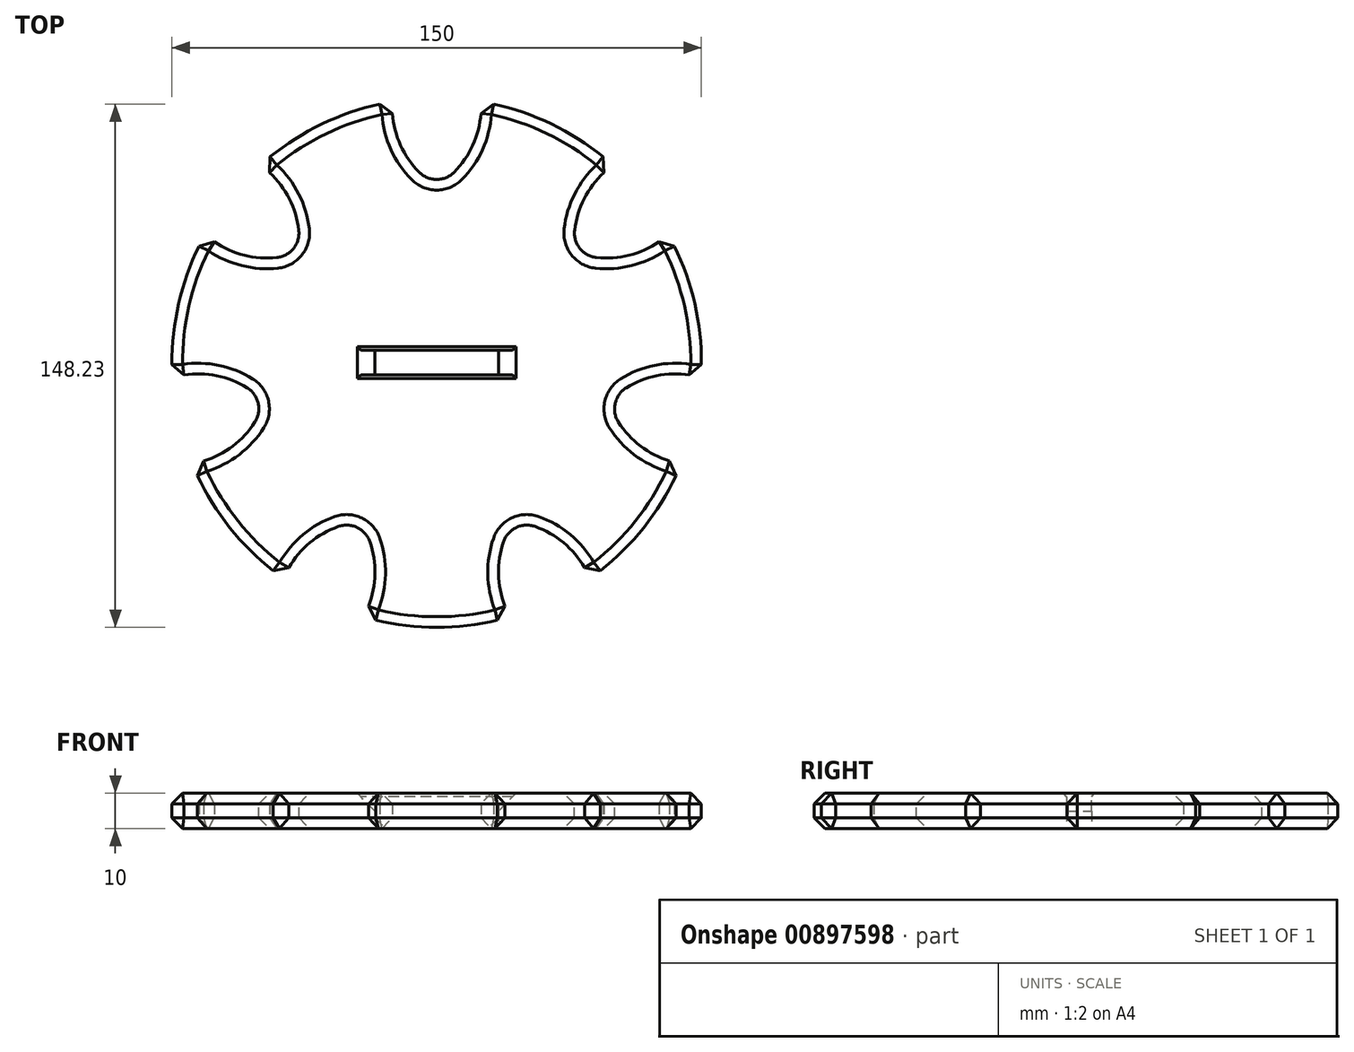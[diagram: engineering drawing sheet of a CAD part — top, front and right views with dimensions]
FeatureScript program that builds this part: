
annotation { "Feature Type Name" : "Feature", "Feature Type Description" : "" }
export const myFeature = defineFeature(function(context is Context, id is Id, definition is map)
    precondition{}
    {
        {
            var Q0;
            Q0=qCreatedBy(makeId("Top.planeOp"),FACE);
            var sketch = newSketch(context, id + "F0", { "sketchPlane" : qUnion([Q0])});
            skCircle(sketch, "E0", {"center": v(0, 0) * mm, "radius": 75 * mm});
            skLineSegment(sketch, "E1", {"start": v(0, 75) * mm, "end": v(0, 50) * mm, "construction": true});
            skLineSegment(sketch, "E2", {"start": v(0, 75) * mm, "end": v(12.5, 75) * mm, "construction": true});
            skLineSegment(sketch, "E3", {"start": v(0, 75) * mm, "end": v(-12.5, 75) * mm, "construction": true});
            skArc(sketch, "E4", {"start": v(-12.5, 75) * mm, "mid": v(-9.82, 60.71) * mm, "end": v(0, 50) * mm});
            skArc(sketch, "E5.MirrorCS", {"start": v(12.5, 75) * mm, "mid": v(9.82, 60.71) * mm, "end": v(0, 50) * mm});
            skLineSegment(sketch, "E6", {"start": v(-12.5, 75) * mm, "end": v(12.5, 75) * mm});
            skArc(sketch, "E7.1.0", {"start": v(-50.84, 56.53) * mm, "mid": v(-41.34, 45.53) * mm, "end": v(-39.1, 31.17) * mm});
            skArc(sketch, "E7.1.1", {"start": v(-66.43, 36.99) * mm, "mid": v(-53.6, 30.17) * mm, "end": v(-39.1, 31.17) * mm});
            skArc(sketch, "E7.2.0", {"start": v(-75.9, -4.5) * mm, "mid": v(-61.38, -3.93) * mm, "end": v(-48.75, -11.13) * mm});
            skArc(sketch, "E7.2.1", {"start": v(-70.34, -28.88) * mm, "mid": v(-57, -23.09) * mm, "end": v(-48.75, -11.13) * mm});
            skArc(sketch, "E7.3.0", {"start": v(-43.8, -62.15) * mm, "mid": v(-35.2, -50.44) * mm, "end": v(-21.7, -45.05) * mm});
            skArc(sketch, "E7.3.1", {"start": v(-21.28, -73) * mm, "mid": v(-17.5, -58.96) * mm, "end": v(-21.7, -45.05) * mm});
            skArc(sketch, "E7.4.0", {"start": v(21.28, -73) * mm, "mid": v(17.5, -58.96) * mm, "end": v(21.7, -45.05) * mm});
            skArc(sketch, "E7.4.1", {"start": v(43.8, -62.15) * mm, "mid": v(35.2, -50.44) * mm, "end": v(21.7, -45.05) * mm});
            skArc(sketch, "E7.5.0", {"start": v(70.34, -28.88) * mm, "mid": v(57, -23.09) * mm, "end": v(48.75, -11.13) * mm});
            skArc(sketch, "E7.5.1", {"start": v(75.9, -4.5) * mm, "mid": v(61.38, -3.93) * mm, "end": v(48.75, -11.13) * mm});
            skArc(sketch, "E7.6.0", {"start": v(66.43, 36.99) * mm, "mid": v(53.6, 30.17) * mm, "end": v(39.1, 31.17) * mm});
            skArc(sketch, "E7.6.1", {"start": v(50.84, 56.53) * mm, "mid": v(41.34, 45.53) * mm, "end": v(39.1, 31.17) * mm});
            skSolve(sketch);
        }
        {
            var Q0;
            {var subQ3=sQuery(id+"F0.wireOp",EDGE,"E0");var subQ22=sQuery(id+"F0.wireOp",EDGE,"E7.6.1");var subQ23=makeQuery(id+"F0.imprint","INTERSECT",VERTEX,{"derivedFrom":[subQ3,subQ22]});Q0=makeQuery(id+"F0.imprint","IMPRINT",FACE,{"disambiguationData":[TD([[makeQuery(id+"F0.imprint","IMPRINT",EDGE,{"disambiguationData":[TD([[subQ23,-1.0]])],"derivedFrom":subQ3}),1.0]])]});}
            extrude(context, id + "F1", {"entities" : qUnion([Q0]), "depth" : 10 * mm, "offsetDistance" : 25 * mm});
        }
        {
            var Q0;
            Q0=makeQuery(id+"F1.opExtrude","SWEPT_EDGE",EDGE,{"disambiguationData":[OSD([sQuery(id+"F0.wireOp",EDGE,"E4"),sQuery(id+"F0.wireOp",EDGE,"E5.MirrorCS")])]});
            var Q1;
            Q1=makeQuery(id+"F1.opExtrude","SWEPT_EDGE",EDGE,{"disambiguationData":[OSD([sQuery(id+"F0.wireOp",EDGE,"E7.6.0"),sQuery(id+"F0.wireOp",EDGE,"E7.6.1")])]});
            var Q2;
            Q2=makeQuery(id+"F1.opExtrude","SWEPT_EDGE",EDGE,{"disambiguationData":[OSD([sQuery(id+"F0.wireOp",EDGE,"E7.1.0"),sQuery(id+"F0.wireOp",EDGE,"E7.1.1")])]});
            var Q3;
            Q3=makeQuery(id+"F1.opExtrude","SWEPT_EDGE",EDGE,{"disambiguationData":[OSD([sQuery(id+"F0.wireOp",EDGE,"E7.2.0"),sQuery(id+"F0.wireOp",EDGE,"E7.2.1")])]});
            var Q4;
            Q4=makeQuery(id+"F1.opExtrude","SWEPT_EDGE",EDGE,{"disambiguationData":[OSD([sQuery(id+"F0.wireOp",EDGE,"E7.3.0"),sQuery(id+"F0.wireOp",EDGE,"E7.3.1")])]});
            var Q5;
            Q5=makeQuery(id+"F1.opExtrude","SWEPT_EDGE",EDGE,{"disambiguationData":[OSD([sQuery(id+"F0.wireOp",EDGE,"E7.4.0"),sQuery(id+"F0.wireOp",EDGE,"E7.4.1")])]});
            var Q6;
            Q6=makeQuery(id+"F1.opExtrude","SWEPT_EDGE",EDGE,{"disambiguationData":[OSD([sQuery(id+"F0.wireOp",EDGE,"E7.5.0"),sQuery(id+"F0.wireOp",EDGE,"E7.5.1")])]});
            fillet(context, id + "F2", {"entities" : qUnion([Q0, Q1, Q2, Q3, Q4, Q5, Q6]), "radius" : 7 * mm, "tangentPropagation" : true, "allowEdgeOverflow" : false});
        }
        {
            var Q0;
            Q0=makeQuery(id+"F1.opExtrude","SWEPT_EDGE",EDGE,{"disambiguationData":[OSD([sQuery(id+"F0.wireOp",EDGE,"E0"),sQuery(id+"F0.wireOp",EDGE,"E7.1.0")])]});
            var Q1;
            Q1=makeQuery(id+"F1.opExtrude","SWEPT_EDGE",EDGE,{"disambiguationData":[OSD([sQuery(id+"F0.wireOp",EDGE,"E0"),sQuery(id+"F0.wireOp",EDGE,"E7.1.1")])]});
            var Q2;
            Q2=makeQuery(id+"F1.opExtrude","SWEPT_EDGE",EDGE,{"disambiguationData":[OSD([sQuery(id+"F0.wireOp",EDGE,"E0"),sQuery(id+"F0.wireOp",EDGE,"E7.2.1")])]});
            var Q3;
            Q3=makeQuery(id+"F1.opExtrude","SWEPT_EDGE",EDGE,{"disambiguationData":[OSD([sQuery(id+"F0.wireOp",EDGE,"E0"),sQuery(id+"F0.wireOp",EDGE,"E7.2.0")])]});
            var Q4;
            Q4=makeQuery(id+"F1.opExtrude","SWEPT_EDGE",EDGE,{"disambiguationData":[OSD([sQuery(id+"F0.wireOp",EDGE,"E0"),sQuery(id+"F0.wireOp",EDGE,"E7.3.0")])]});
            var Q5;
            Q5=makeQuery(id+"F1.opExtrude","SWEPT_EDGE",EDGE,{"disambiguationData":[OSD([sQuery(id+"F0.wireOp",EDGE,"E0"),sQuery(id+"F0.wireOp",EDGE,"E7.3.1")])]});
            var Q6;
            Q6=makeQuery(id+"F1.opExtrude","SWEPT_EDGE",EDGE,{"disambiguationData":[OSD([sQuery(id+"F0.wireOp",EDGE,"E0"),sQuery(id+"F0.wireOp",EDGE,"E7.4.0")])]});
            var Q7;
            Q7=makeQuery(id+"F1.opExtrude","SWEPT_EDGE",EDGE,{"disambiguationData":[OSD([sQuery(id+"F0.wireOp",EDGE,"E0"),sQuery(id+"F0.wireOp",EDGE,"E7.4.1")])]});
            var Q8;
            Q8=makeQuery(id+"F1.opExtrude","SWEPT_EDGE",EDGE,{"disambiguationData":[OSD([sQuery(id+"F0.wireOp",EDGE,"E0"),sQuery(id+"F0.wireOp",EDGE,"E7.5.0")])]});
            var Q9;
            Q9=makeQuery(id+"F1.opExtrude","SWEPT_EDGE",EDGE,{"disambiguationData":[OSD([sQuery(id+"F0.wireOp",EDGE,"E0"),sQuery(id+"F0.wireOp",EDGE,"E7.5.1")])]});
            var Q10;
            Q10=makeQuery(id+"F1.opExtrude","SWEPT_EDGE",EDGE,{"disambiguationData":[OSD([sQuery(id+"F0.wireOp",EDGE,"E0"),sQuery(id+"F0.wireOp",EDGE,"E7.6.0")])]});
            var Q11;
            Q11=makeQuery(id+"F1.opExtrude","CAP_EDGE",EDGE,{"disambiguationData":[OSD([sQuery(id+"F0.wireOp",EDGE,"E7.6.1")])],"isStart":false});
            var Q12;
            Q12=makeQuery(id+"F1.opExtrude","SWEPT_EDGE",EDGE,{"disambiguationData":[OSD([sQuery(id+"F0.wireOp",EDGE,"E0"),sQuery(id+"F0.wireOp",EDGE,"E7.6.1")])]});
            var Q13;
            Q13=makeQuery(id+"F1.opExtrude","SWEPT_EDGE",EDGE,{"disambiguationData":[OSD([sQuery(id+"F0.wireOp",EDGE,"E0"),sQuery(id+"F0.wireOp",EDGE,"E4")])]});
            var Q14;
            Q14=makeQuery(id+"F1.opExtrude","SWEPT_EDGE",EDGE,{"disambiguationData":[OSD([sQuery(id+"F0.wireOp",EDGE,"E0"),sQuery(id+"F0.wireOp",EDGE,"E5.MirrorCS")])]});
            var Q15;
            Q15=makeQuery(id+"F1.opExtrude","CAP_EDGE",EDGE,{"disambiguationData":[OSD([sQuery(id+"F0.wireOp",EDGE,"E5.MirrorCS")])],"isStart":false});
            var Q16;
            Q16=makeQuery(id+"F1.opExtrude","CAP_EDGE",EDGE,{"disambiguationData":[OSD([sQuery(id+"F0.wireOp",EDGE,"E7.1.0")])],"isStart":false});
            var Q17;
            Q17=makeQuery(id+"F1.opExtrude","CAP_EDGE",EDGE,{"disambiguationData":[OSD([sQuery(id+"F0.wireOp",EDGE,"E7.2.0")])],"isStart":false});
            var Q18;
            Q18=makeQuery(id+"F1.opExtrude","CAP_EDGE",EDGE,{"disambiguationData":[OSD([sQuery(id+"F0.wireOp",EDGE,"E7.3.0")])],"isStart":false});
            var Q19;
            Q19=makeQuery(id+"F1.opExtrude","CAP_EDGE",EDGE,{"disambiguationData":[OSD([sQuery(id+"F0.wireOp",EDGE,"E7.4.0")])],"isStart":false});
            var Q20;
            Q20=makeQuery(id+"F1.opExtrude","CAP_EDGE",EDGE,{"disambiguationData":[OSD([sQuery(id+"F0.wireOp",EDGE,"E7.5.0")])],"isStart":false});
            var Q21;
            Q21=makeQuery(id+"F1.opExtrude","CAP_FACE",FACE,{"disambiguationData":[OSD([sQuery(id+"F0.wireOp",EDGE,"E0"),sQuery(id+"F0.wireOp",EDGE,"E4"),sQuery(id+"F0.wireOp",EDGE,"E5.MirrorCS"),sQuery(id+"F0.wireOp",EDGE,"E7.1.0"),sQuery(id+"F0.wireOp",EDGE,"E7.1.1"),sQuery(id+"F0.wireOp",EDGE,"E7.2.0"),sQuery(id+"F0.wireOp",EDGE,"E7.2.1"),sQuery(id+"F0.wireOp",EDGE,"E7.3.0"),sQuery(id+"F0.wireOp",EDGE,"E7.3.1"),sQuery(id+"F0.wireOp",EDGE,"E7.4.0"),sQuery(id+"F0.wireOp",EDGE,"E7.4.1"),sQuery(id+"F0.wireOp",EDGE,"E7.5.0"),sQuery(id+"F0.wireOp",EDGE,"E7.5.1"),sQuery(id+"F0.wireOp",EDGE,"E7.6.0"),sQuery(id+"F0.wireOp",EDGE,"E7.6.1")])],"isStart":true});
            var Q22;
            Q22=makeQuery(id+"F1.opExtrude","CAP_FACE",FACE,{"disambiguationData":[OSD([sQuery(id+"F0.wireOp",EDGE,"E0"),sQuery(id+"F0.wireOp",EDGE,"E4"),sQuery(id+"F0.wireOp",EDGE,"E5.MirrorCS"),sQuery(id+"F0.wireOp",EDGE,"E7.1.0"),sQuery(id+"F0.wireOp",EDGE,"E7.1.1"),sQuery(id+"F0.wireOp",EDGE,"E7.2.0"),sQuery(id+"F0.wireOp",EDGE,"E7.2.1"),sQuery(id+"F0.wireOp",EDGE,"E7.3.0"),sQuery(id+"F0.wireOp",EDGE,"E7.3.1"),sQuery(id+"F0.wireOp",EDGE,"E7.4.0"),sQuery(id+"F0.wireOp",EDGE,"E7.4.1"),sQuery(id+"F0.wireOp",EDGE,"E7.5.0"),sQuery(id+"F0.wireOp",EDGE,"E7.5.1"),sQuery(id+"F0.wireOp",EDGE,"E7.6.0"),sQuery(id+"F0.wireOp",EDGE,"E7.6.1")])],"isStart":false});
            chamfer(context, id + "F3", {"entities" : qUnion([Q0, Q1, Q2, Q3, Q4, Q5, Q6, Q7, Q8, Q9, Q10, Q11, Q12, Q13, Q14, Q15, Q16, Q17, Q18, Q19, Q20, Q21, Q22]), "width" : 3 * mm, "tangentPropagation" : true});
        }
        {
            var Q0;
            Q0=makeQuery(id+"F1.opExtrude","CAP_FACE",FACE,{"disambiguationData":[OSD([sQuery(id+"F0.wireOp",EDGE,"E0"),sQuery(id+"F0.wireOp",EDGE,"E4"),sQuery(id+"F0.wireOp",EDGE,"E5.MirrorCS"),sQuery(id+"F0.wireOp",EDGE,"E7.1.0"),sQuery(id+"F0.wireOp",EDGE,"E7.1.1"),sQuery(id+"F0.wireOp",EDGE,"E7.2.0"),sQuery(id+"F0.wireOp",EDGE,"E7.2.1"),sQuery(id+"F0.wireOp",EDGE,"E7.3.0"),sQuery(id+"F0.wireOp",EDGE,"E7.3.1"),sQuery(id+"F0.wireOp",EDGE,"E7.4.0"),sQuery(id+"F0.wireOp",EDGE,"E7.4.1"),sQuery(id+"F0.wireOp",EDGE,"E7.5.0"),sQuery(id+"F0.wireOp",EDGE,"E7.5.1"),sQuery(id+"F0.wireOp",EDGE,"E7.6.0"),sQuery(id+"F0.wireOp",EDGE,"E7.6.1")])],"isStart":false});
            var sketch = newSketch(context, id + "F4", { "sketchPlane" : qUnion([Q0])});
            skSolve(sketch);
        }
        {
            var Q0;
            {var subQ0=sQuery(id+"F0.wireOp",EDGE,"E7.6.1");var subQ1=sQuery(id+"F0.wireOp",EDGE,"E7.6.0");var subQ2=sQuery(id+"F0.wireOp",EDGE,"E7.5.1");var subQ3=sQuery(id+"F0.wireOp",EDGE,"E7.5.0");var subQ4=sQuery(id+"F0.wireOp",EDGE,"E7.4.1");var subQ5=sQuery(id+"F0.wireOp",EDGE,"E7.4.0");var subQ6=sQuery(id+"F0.wireOp",EDGE,"E7.3.1");var subQ7=sQuery(id+"F0.wireOp",EDGE,"E7.3.0");var subQ8=sQuery(id+"F0.wireOp",EDGE,"E7.2.1");var subQ9=sQuery(id+"F0.wireOp",EDGE,"E7.2.0");var subQ10=sQuery(id+"F0.wireOp",EDGE,"E7.1.1");var subQ11=sQuery(id+"F0.wireOp",EDGE,"E7.1.0");var subQ12=sQuery(id+"F0.wireOp",EDGE,"E5.MirrorCS");var subQ13=sQuery(id+"F0.wireOp",EDGE,"E4");var subQ14=sQuery(id+"F0.wireOp",EDGE,"E0");var subQ15=makeQuery(id+"F1.opExtrude","CAP_FACE",FACE,{"disambiguationData":[OSD([subQ14,subQ13,subQ12,subQ11,subQ10,subQ9,subQ8,subQ7,subQ6,subQ5,subQ4,subQ3,subQ2,subQ1,subQ0])],"isStart":false});var subQ16=subQ15;Q0=makeQuery(id+"F4.imprint","IMPRINT",FACE,{"disambiguationData":[TD([[makeQuery(id+"F4.imprint","IMPRINT",EDGE,{"derivedFrom":makeQuery(id+"F3.opChamfer","BLEND_EDGE",EDGE,{"blendedFrom":[makeQuery(id+"F1.opExtrude","CAP_EDGE",EDGE,{"disambiguationData":[OSD([subQ13])],"isStart":false}),subQ16],"blendedInto":[subQ16]})}),1.0]])]});}
            var sketch = newSketch(context, id + "F5", { "sketchPlane" : qUnion([Q0])});
            skLineSegment(sketch, "E8.bottom", {"start": v(17.5, 3.5) * mm, "end": v(-17.5, 3.5) * mm});
            skLineSegment(sketch, "E8.top", {"start": v(17.5, -3.5) * mm, "end": v(-17.5, -3.5) * mm});
            skLineSegment(sketch, "E8.left", {"start": v(17.5, 3.5) * mm, "end": v(17.5, -3.5) * mm});
            skLineSegment(sketch, "E8.right", {"start": v(-17.5, 3.5) * mm, "end": v(-17.5, -3.5) * mm});
            skPoint(sketch, "E8.middle", {"position": v(0, 0) * mm});
            skLineSegment(sketch, "E9", {"start": v(-17.5, -3.5) * mm, "end": v(-17.5, 3.5) * mm});
            skLineSegment(sketch, "E10", {"start": v(-17.5, 3.5) * mm, "end": v(17.5, 3.5) * mm});
            skSolve(sketch);
        }
        {
            var Q0;
            Q0=makeQuery(id+"F1.opExtrude","CAP_FACE",FACE,{"disambiguationData":[OSD([sQuery(id+"F0.wireOp",EDGE,"E0"),sQuery(id+"F0.wireOp",EDGE,"E4"),sQuery(id+"F0.wireOp",EDGE,"E5.MirrorCS"),sQuery(id+"F0.wireOp",EDGE,"E7.1.0"),sQuery(id+"F0.wireOp",EDGE,"E7.1.1"),sQuery(id+"F0.wireOp",EDGE,"E7.2.0"),sQuery(id+"F0.wireOp",EDGE,"E7.2.1"),sQuery(id+"F0.wireOp",EDGE,"E7.3.0"),sQuery(id+"F0.wireOp",EDGE,"E7.3.1"),sQuery(id+"F0.wireOp",EDGE,"E7.4.0"),sQuery(id+"F0.wireOp",EDGE,"E7.4.1"),sQuery(id+"F0.wireOp",EDGE,"E7.5.0"),sQuery(id+"F0.wireOp",EDGE,"E7.5.1"),sQuery(id+"F0.wireOp",EDGE,"E7.6.0"),sQuery(id+"F0.wireOp",EDGE,"E7.6.1")])],"isStart":true});
            var sketch = newSketch(context, id + "F6", { "sketchPlane" : qUnion([Q0])});
            skLineSegment(sketch, "E11.bottom", {"start": v(17.5, -3.5) * mm, "end": v(-17.5, -3.5) * mm});
            skLineSegment(sketch, "E11.top", {"start": v(17.5, 3.5) * mm, "end": v(-17.5, 3.5) * mm});
            skLineSegment(sketch, "E11.left", {"start": v(17.5, -3.5) * mm, "end": v(17.5, 3.5) * mm});
            skLineSegment(sketch, "E11.right", {"start": v(-17.5, -3.5) * mm, "end": v(-17.5, 3.5) * mm});
            skPoint(sketch, "E11.middle", {"position": v(0, 0) * mm});
            skSolve(sketch);
        }
        {
            var Q0;
            Q0=makeQuery(id+"F6.imprint","IMPRINT",FACE,{"disambiguationData":[TD([[makeQuery(id+"F6.imprint","IMPRINT",EDGE,{"derivedFrom":sQuery(id+"F6.wireOp",EDGE,"E11.bottom")}),-1.0]])]});
            extrude(context, id + "F7", {"entities" : qUnion([Q0]), "operationType" : NewBodyOperationType.REMOVE, "oppositeDirection" : true, "depth" : 25 * mm, "offsetDistance" : 25 * mm});
        }
        {
            var Q0;
            Q0=makeQuery(id+"F7.boolean.opBoolean","INTERSECT",EDGE,{"derivedFrom":[makeQuery(id+"F1.opExtrude","CAP_FACE",FACE,{"disambiguationData":[OSD([sQuery(id+"F0.wireOp",EDGE,"E0"),sQuery(id+"F0.wireOp",EDGE,"E4"),sQuery(id+"F0.wireOp",EDGE,"E5.MirrorCS"),sQuery(id+"F0.wireOp",EDGE,"E7.1.0"),sQuery(id+"F0.wireOp",EDGE,"E7.1.1"),sQuery(id+"F0.wireOp",EDGE,"E7.2.0"),sQuery(id+"F0.wireOp",EDGE,"E7.2.1"),sQuery(id+"F0.wireOp",EDGE,"E7.3.0"),sQuery(id+"F0.wireOp",EDGE,"E7.3.1"),sQuery(id+"F0.wireOp",EDGE,"E7.4.0"),sQuery(id+"F0.wireOp",EDGE,"E7.4.1"),sQuery(id+"F0.wireOp",EDGE,"E7.5.0"),sQuery(id+"F0.wireOp",EDGE,"E7.5.1"),sQuery(id+"F0.wireOp",EDGE,"E7.6.0"),sQuery(id+"F0.wireOp",EDGE,"E7.6.1")])],"isStart":false}),makeQuery(id+"F7.opExtrude","SWEPT_FACE",FACE,{"disambiguationData":[OSD([sQuery(id+"F6.wireOp",EDGE,"E11.right")])]})]});
            var Q1;
            Q1=makeQuery(id+"F7.boolean.opBoolean","INTERSECT",EDGE,{"derivedFrom":[makeQuery(id+"F1.opExtrude","CAP_FACE",FACE,{"disambiguationData":[OSD([sQuery(id+"F0.wireOp",EDGE,"E0"),sQuery(id+"F0.wireOp",EDGE,"E4"),sQuery(id+"F0.wireOp",EDGE,"E5.MirrorCS"),sQuery(id+"F0.wireOp",EDGE,"E7.1.0"),sQuery(id+"F0.wireOp",EDGE,"E7.1.1"),sQuery(id+"F0.wireOp",EDGE,"E7.2.0"),sQuery(id+"F0.wireOp",EDGE,"E7.2.1"),sQuery(id+"F0.wireOp",EDGE,"E7.3.0"),sQuery(id+"F0.wireOp",EDGE,"E7.3.1"),sQuery(id+"F0.wireOp",EDGE,"E7.4.0"),sQuery(id+"F0.wireOp",EDGE,"E7.4.1"),sQuery(id+"F0.wireOp",EDGE,"E7.5.0"),sQuery(id+"F0.wireOp",EDGE,"E7.5.1"),sQuery(id+"F0.wireOp",EDGE,"E7.6.0"),sQuery(id+"F0.wireOp",EDGE,"E7.6.1")])],"isStart":false}),makeQuery(id+"F7.opExtrude","SWEPT_FACE",FACE,{"disambiguationData":[OSD([sQuery(id+"F6.wireOp",EDGE,"E11.left")])]})]});
            chamfer(context, id + "F8", {"entities" : qUnion([Q0, Q1]), "width" : 5 * mm, "tangentPropagation" : true});
        }
        {
            var Q0;
            Q0=makeQuery(id+"F7.boolean.opBoolean","INTERSECT",EDGE,{"derivedFrom":[makeQuery(id+"F1.opExtrude","CAP_FACE",FACE,{"disambiguationData":[OSD([sQuery(id+"F0.wireOp",EDGE,"E0"),sQuery(id+"F0.wireOp",EDGE,"E4"),sQuery(id+"F0.wireOp",EDGE,"E5.MirrorCS"),sQuery(id+"F0.wireOp",EDGE,"E7.1.0"),sQuery(id+"F0.wireOp",EDGE,"E7.1.1"),sQuery(id+"F0.wireOp",EDGE,"E7.2.0"),sQuery(id+"F0.wireOp",EDGE,"E7.2.1"),sQuery(id+"F0.wireOp",EDGE,"E7.3.0"),sQuery(id+"F0.wireOp",EDGE,"E7.3.1"),sQuery(id+"F0.wireOp",EDGE,"E7.4.0"),sQuery(id+"F0.wireOp",EDGE,"E7.4.1"),sQuery(id+"F0.wireOp",EDGE,"E7.5.0"),sQuery(id+"F0.wireOp",EDGE,"E7.5.1"),sQuery(id+"F0.wireOp",EDGE,"E7.6.0"),sQuery(id+"F0.wireOp",EDGE,"E7.6.1")])],"isStart":false}),makeQuery(id+"F7.opExtrude","SWEPT_FACE",FACE,{"disambiguationData":[OSD([sQuery(id+"F6.wireOp",EDGE,"E11.bottom")])]})]});
            var Q1;
            Q1=makeQuery(id+"F7.boolean.opBoolean","INTERSECT",EDGE,{"derivedFrom":[makeQuery(id+"F1.opExtrude","CAP_FACE",FACE,{"disambiguationData":[OSD([sQuery(id+"F0.wireOp",EDGE,"E0"),sQuery(id+"F0.wireOp",EDGE,"E4"),sQuery(id+"F0.wireOp",EDGE,"E5.MirrorCS"),sQuery(id+"F0.wireOp",EDGE,"E7.1.0"),sQuery(id+"F0.wireOp",EDGE,"E7.1.1"),sQuery(id+"F0.wireOp",EDGE,"E7.2.0"),sQuery(id+"F0.wireOp",EDGE,"E7.2.1"),sQuery(id+"F0.wireOp",EDGE,"E7.3.0"),sQuery(id+"F0.wireOp",EDGE,"E7.3.1"),sQuery(id+"F0.wireOp",EDGE,"E7.4.0"),sQuery(id+"F0.wireOp",EDGE,"E7.4.1"),sQuery(id+"F0.wireOp",EDGE,"E7.5.0"),sQuery(id+"F0.wireOp",EDGE,"E7.5.1"),sQuery(id+"F0.wireOp",EDGE,"E7.6.0"),sQuery(id+"F0.wireOp",EDGE,"E7.6.1")])],"isStart":false}),makeQuery(id+"F7.opExtrude","SWEPT_FACE",FACE,{"disambiguationData":[OSD([sQuery(id+"F6.wireOp",EDGE,"E11.top")])]})]});
            chamfer(context, id + "F9", {"entities" : qUnion([Q0, Q1]), "width" : 1 * mm, "tangentPropagation" : true});
        }
    });
